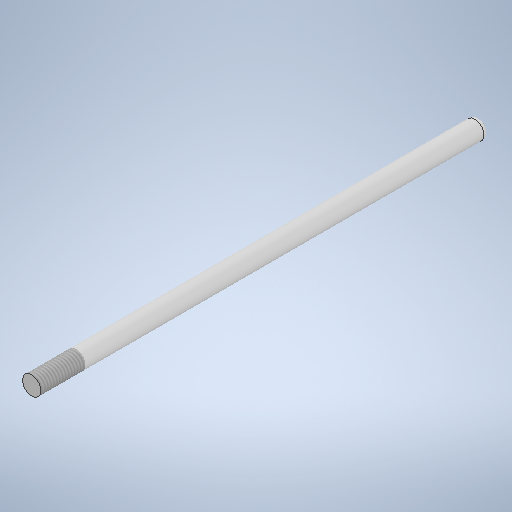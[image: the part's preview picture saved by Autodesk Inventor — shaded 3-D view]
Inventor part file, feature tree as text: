
AUTODESK INVENTOR PART (.ipt)
format: ipt  version: 2025 (Build 290162010, 162A)  size: 255,488 bytes
history: native  units: mm
features: extrude x1, fillet x1, thread x1, sketch x1
ambient origin geometry x8: Origin, YZ Plane, XZ Plane, XY Plane, X Axis, Y Axis, Z Axis, Center Point
bodies: Solid1 (feature_tree)
feature tree (4):
  extrude  "Extrusion1"  Depth=121.0mm TaperAngle=0.0deg
  fillet  "Fillet1"  Radius=1.5mm
  thread  "Thread1"  [1 undecoded]
  sketch  "Sketch1"  dims[d0=5.0mm d1=121.0mm d2=0.0mm d3=1.5mm d4=12.0mm d5=0.0mm]
note: 1 required parameter value undecoded (feature->parameter linkage not recoverable at this tier; creation-order binding heuristic only, values carry confidence <= 0.55)
